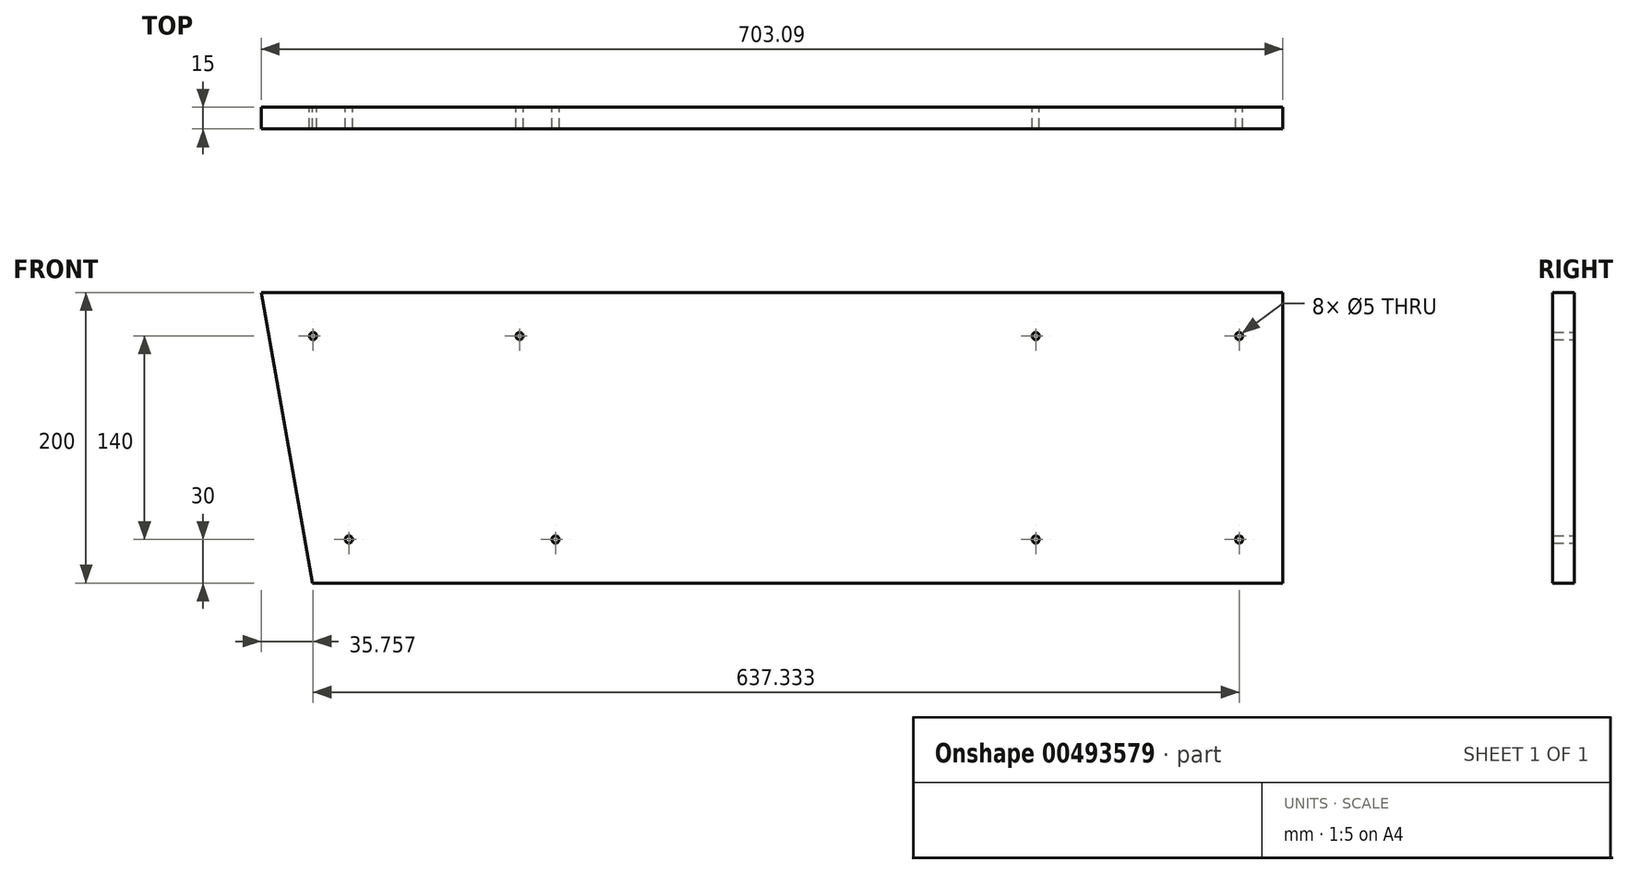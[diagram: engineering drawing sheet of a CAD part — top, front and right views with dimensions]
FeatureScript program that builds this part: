
annotation { "Feature Type Name" : "Feature", "Feature Type Description" : "" }
export const myFeature = defineFeature(function(context is Context, id is Id, definition is map)
    precondition{}
    {
        {
            var Q0;
            Q0=qCreatedBy(makeId("Front.planeOp"),FACE);
            var sketch = newSketch(context, id + "F0", { "sketchPlane" : qUnion([Q0])});
            skLineSegment(sketch, "E0", {"start": v(0, 0) * mm, "end": v(0, 200) * mm});
            skLineSegment(sketch, "E1", {"start": v(0, 200) * mm, "end": v(-703.09, 200) * mm});
            skLineSegment(sketch, "E2", {"start": v(-703.09, 200) * mm, "end": v(-667.82, 0) * mm});
            skLineSegment(sketch, "E3", {"start": v(-667.82, 0) * mm, "end": v(0, 0) * mm});
            skLineSegment(sketch, "E4", {"start": v(-464.73, 0) * mm, "end": v(-500, 200) * mm, "construction": true});
            skLineSegment(sketch, "E5.0", {"start": v(0, 170) * mm, "end": v(-703.09, 170) * mm, "construction": true});
            skLineSegment(sketch, "E6.0", {"start": v(-494.28, -5.2) * mm, "end": v(-529.54, 194.8) * mm, "construction": true});
            skLineSegment(sketch, "E7.0", {"start": v(-667.82, 30) * mm, "end": v(0, 30) * mm, "construction": true});
            skLineSegment(sketch, "E8.0", {"start": v(-673.54, 205.2) * mm, "end": v(-638.28, 5.2) * mm, "construction": true});
            skCircle(sketch, "E9", {"center": v(-667.33, 170) * mm, "radius": 2.5 * mm});
            skCircle(sketch, "E10", {"center": v(-525.17, 170) * mm, "radius": 2.5 * mm});
            skCircle(sketch, "E11", {"center": v(-500.49, 30) * mm, "radius": 2.5 * mm});
            skCircle(sketch, "E12", {"center": v(-642.65, 30) * mm, "radius": 2.5 * mm});
            skLineSegment(sketch, "E13.0", {"start": v(-30, 0) * mm, "end": v(-30, 200) * mm, "construction": true});
            skLineSegment(sketch, "E14.0", {"start": v(-170, 0) * mm, "end": v(-170, 200) * mm, "construction": true});
            skCircle(sketch, "E15", {"center": v(-170, 170) * mm, "radius": 2.5 * mm});
            skCircle(sketch, "E16", {"center": v(-30, 170) * mm, "radius": 2.5 * mm});
            skCircle(sketch, "E17", {"center": v(-30, 30) * mm, "radius": 2.5 * mm});
            skCircle(sketch, "E18", {"center": v(-170, 30) * mm, "radius": 2.5 * mm});
            skSolve(sketch);
        }
        {
            var Q0;
            Q0=makeQuery(id+"F0.imprint","IMPRINT",FACE,{"disambiguationData":[TD([[makeQuery(id+"F0.imprint","IMPRINT",EDGE,{"derivedFrom":sQuery(id+"F0.wireOp",EDGE,"E0")}),1.0]])]});
            extrude(context, id + "F1", {"entities" : qUnion([Q0]), "endBound" : BoundingType.SYMMETRIC, "depth" : 15 * mm});
        }
    });
